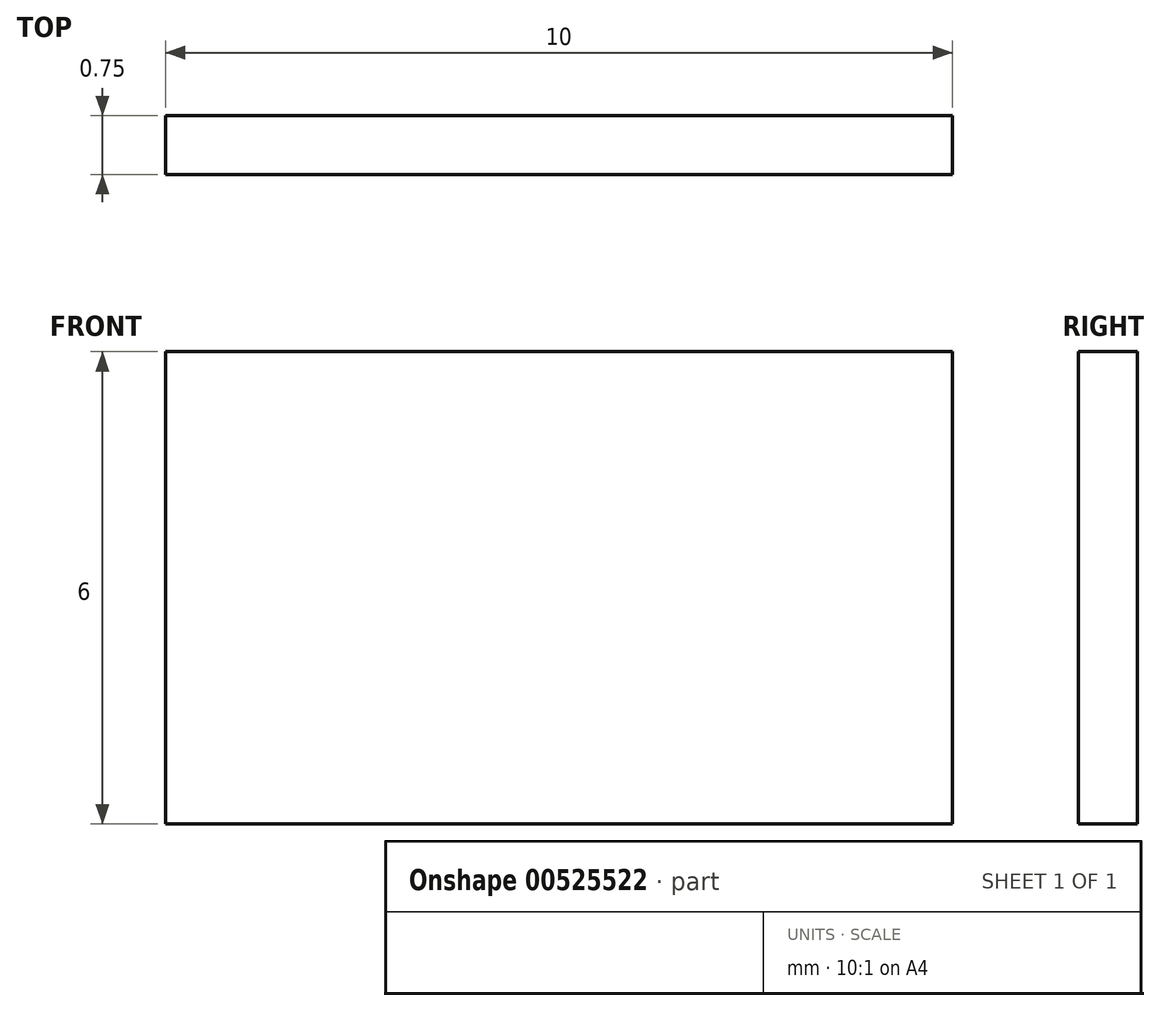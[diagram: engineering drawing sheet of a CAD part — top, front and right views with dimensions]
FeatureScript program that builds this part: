
annotation { "Feature Type Name" : "Feature", "Feature Type Description" : "" }
export const myFeature = defineFeature(function(context is Context, id is Id, definition is map)
    precondition{}
    {
        {
            var Q0;
            Q0=qCreatedBy(makeId("Front.planeOp"),FACE);
            var sketch = newSketch(context, id + "F0", { "sketchPlane" : qUnion([Q0])});
            skLineSegment(sketch, "E0.bottom", {"start": v(0, 0) * mm, "end": v(10, 0) * mm});
            skLineSegment(sketch, "E0.top", {"start": v(0, -6) * mm, "end": v(10, -6) * mm});
            skLineSegment(sketch, "E0.left", {"start": v(0, 0) * mm, "end": v(0, -6) * mm});
            skLineSegment(sketch, "E0.right", {"start": v(10, 0) * mm, "end": v(10, -6) * mm});
            skSolve(sketch);
        }
        {
            var Q0;
            Q0=makeQuery(id+"F0.imprint","IMPRINT",FACE,{"disambiguationData":[TD([[makeQuery(id+"F0.imprint","IMPRINT",EDGE,{"derivedFrom":sQuery(id+"F0.wireOp",EDGE,"E0.bottom")}),-1.0]])]});
            extrude(context, id + "F1", {"entities" : qUnion([Q0]), "depth" : .75 * mm, "offsetDistance" : 25.4 * mm});
        }
    });
